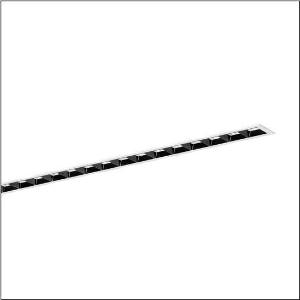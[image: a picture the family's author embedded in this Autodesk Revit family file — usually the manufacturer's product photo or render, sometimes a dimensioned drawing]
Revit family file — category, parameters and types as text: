
# Revit family: silica_r__21_51mx14da44wb_4ffe
name_source: partatom
category: Lighting Fixtures
units: mm (PartAtom-declared; Revit-internal decimal feet)

## family parameters
Cut with Voids When Loaded = No
Host = Face
Light Source = No
Part Type = Normal
Room Calculation Point = No
Round Connector Dimension = Use Diameter
Shared = No

## types (1)
- --- (1 x LED, 4320 lm, 30 W, 4000K)
    Apparent Load = 30 VA
    CIE Flux Codes = 74 94 99 100 100
    Color Rendering = 80
    Color Temperature = 4000K
    Default Elevation = 1800 mm
    Description = Silica® 21, office luminaire, primary light control with darklight reflector, of PMMA, black, light emission: direct distribution, primary light characteristic: asymmetric, installation type: recessed, LED, rated luminous flux: 4.320lm, luminous efficacy: 144lm/W, light colour: 840, colour temperature: 4000K, with terminal, 3+2-pole, max. 2.5mm², mains connection: 220..240V, AC, 50/60Hz, rated input power: 30W, luminaire housing, of aluminium, traffic white (RAL 9016), length: 1.228mm, width: 79mm, height: 53mm, protection rating (complete): IP20, insulation class (complete): insulation class I (protective earthing), certification: CE, permissible operating ambient temperature: 0..+35°C, standard: EN 50419, packaging unit: 1 piece
    Height = 0 mm  [stored 0 ft]
    Lamp = 1 x LED
    Lamp Light Flux = 4320 lm
    Lamp Power = 30 W
    Lamp count = 1
    Length = 1227 mm
    Luminous efficacy = 144 lm/W
    Manufacturer = Siteco
    ModVariant = No
    Model = 51MX14DA44WB
    Mounting Place = Ceiling
    Mounting Type = Recessed
    Number of Poles = 1
    OnlyDefault = Yes
    Power Factor = 1
    Product Name = Silica® 21
    Product group = office luminaire | ceiling recessed
    ProductGroupID = 401
    Protection Class = Protection class I
    Protection Degree = IP 20
    RLX_Detail_Level = 1
    RLX_Emergency_Light_Flux = 0 lm
    RLX_Emergency_Type = 0
    RLX_Emergency_Type_DB = No
    RlxData = <blob elided: 38957 chars, md5=067e0b98>
    Socket = socket
    Standby Power = 0 W
    System Light Flux = 4320 lm
    System Power = 30 W
    Type Comments = factory setting: luminous flux: 100 % | dim-lin: 254 | 418 mA
    Type Image = l_1297791.jpg
    URL = http://relux.com
    VarID = @adj_053225
    Voltage = 0 V
    Weight = 0.00 kg
    Width = 79 mm

note: [stored X ft] marks values corroborated as IEEE doubles in the binary element streams (Revit-internal decimal feet)

## geometry (parser evidence)
native form markers: Blend x4, Sweep x9
no freeform markers — native parametric forms only
